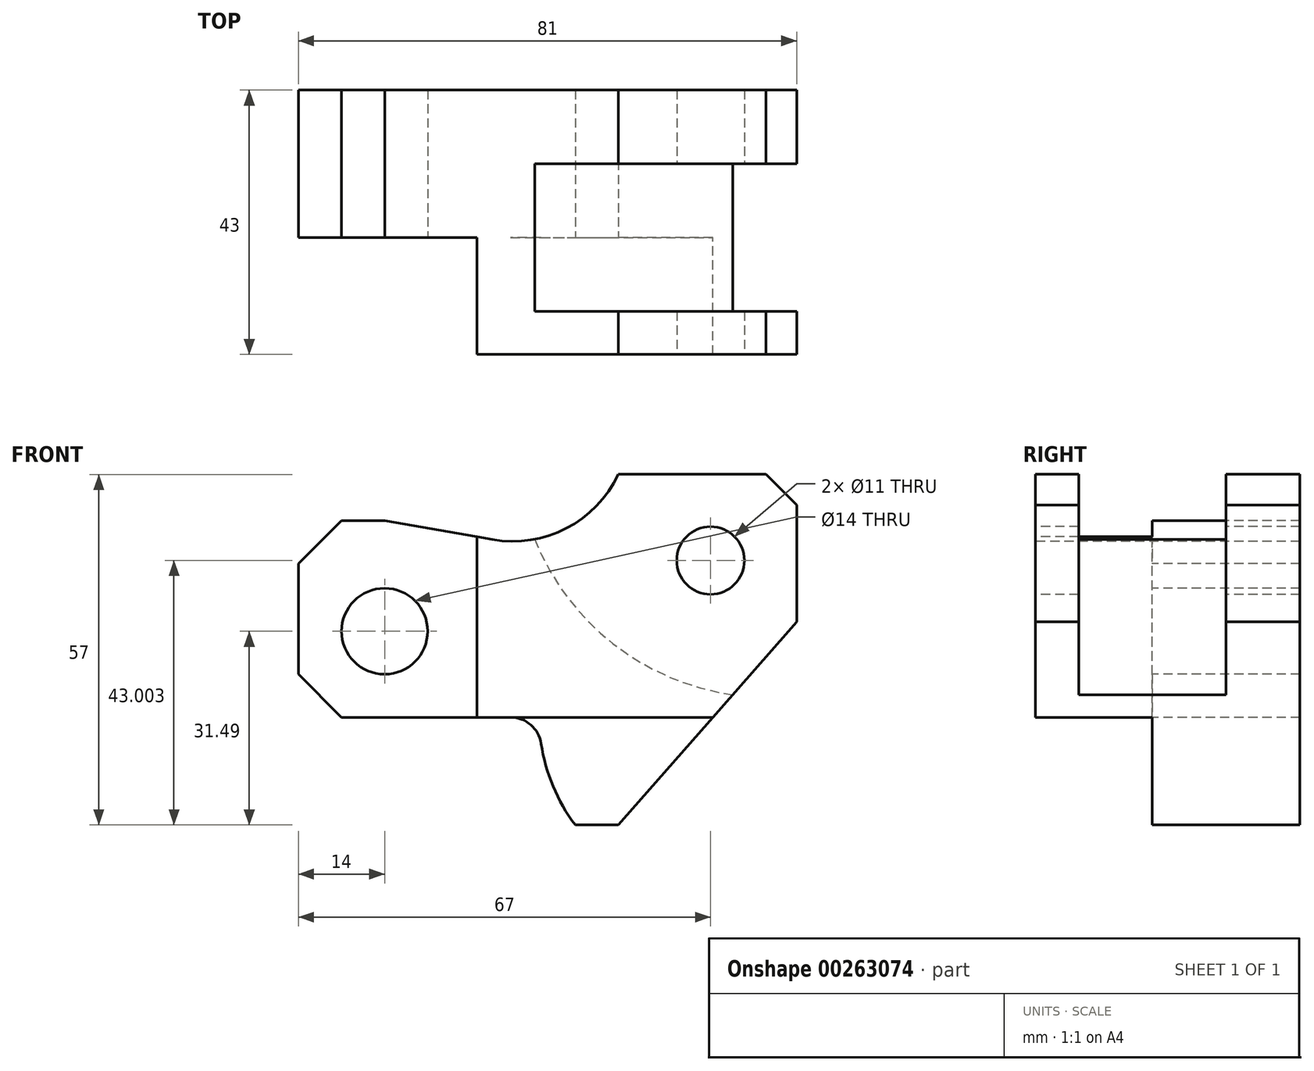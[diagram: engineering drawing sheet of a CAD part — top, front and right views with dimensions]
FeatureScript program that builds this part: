
annotation { "Feature Type Name" : "Feature", "Feature Type Description" : "" }
export const myFeature = defineFeature(function(context is Context, id is Id, definition is map)
    precondition{}
    {
        {
            var Q0;
            Q0=qCreatedBy(makeId("Front.planeOp"),FACE);
            var sketch = newSketch(context, id + "F0", { "sketchPlane" : qUnion([Q0])});
            skCircle(sketch, "E0", {"center": v(0, 0) * mm, "radius": 7 * mm});
            skLineSegment(sketch, "E1", {"start": v(0, 18) * mm, "end": v(-7, 18) * mm});
            skLineSegment(sketch, "E2", {"start": v(-7, -14) * mm, "end": v(-14, -7) * mm});
            skLineSegment(sketch, "E3", {"start": v(-14, -7) * mm, "end": v(-14, 11) * mm});
            skLineSegment(sketch, "E4", {"start": v(-14, 11) * mm, "end": v(-7, 18) * mm});
            skLineSegment(sketch, "E5", {"start": v(38, -31.49) * mm, "end": v(31, -31.49) * mm});
            skArc(sketch, "E6", {"start": v(25.45, -18.26) * mm, "mid": v(27.4, -25.22) * mm, "end": v(31, -31.49) * mm});
            skArc(sketch, "E7", {"start": v(25.45, -18.26) * mm, "mid": v(23.77, -15.21) * mm, "end": v(20.5, -14) * mm});
            skLineSegment(sketch, "E8", {"start": v(-7, -14) * mm, "end": v(20.5, -14) * mm});
            skLineSegment(sketch, "E9", {"start": v(38, -31.49) * mm, "end": v(67, 1.51) * mm});
            skLineSegment(sketch, "E10", {"start": v(67, 1.51) * mm, "end": v(67, 20.51) * mm});
            skLineSegment(sketch, "E11", {"start": v(62, 25.51) * mm, "end": v(67, 20.51) * mm});
            skLineSegment(sketch, "E12", {"start": v(62, 25.51) * mm, "end": v(38, 25.51) * mm});
            skArc(sketch, "E13", {"start": v(17.52, 14.91) * mm, "mid": v(29.55, 16.75) * mm, "end": v(38, 25.51) * mm});
            skLineSegment(sketch, "E14", {"start": v(0, 18) * mm, "end": v(17.52, 14.91) * mm});
            skSolve(sketch);
        }
        {
            var Q0;
            Q0=makeQuery(id+"F0.imprint","IMPRINT",FACE,{"disambiguationData":[TD([[makeQuery(id+"F0.imprint","IMPRINT",EDGE,{"derivedFrom":sQuery(id+"F0.wireOp",EDGE,"E0")}),-1.0]])]});
            extrude(context, id + "F1", {"entities" : qUnion([Q0]), "oppositeDirection" : true, "depth" : 43 * mm});
        }
        {
            var Q0;
            Q0=makeQuery(id+"F1.opExtrude","CAP_FACE",FACE,{"disambiguationData":[OSD([sQuery(id+"F0.wireOp",EDGE,"E0"),sQuery(id+"F0.wireOp",EDGE,"E1"),sQuery(id+"F0.wireOp",EDGE,"E2"),sQuery(id+"F0.wireOp",EDGE,"E3"),sQuery(id+"F0.wireOp",EDGE,"E4"),sQuery(id+"F0.wireOp",EDGE,"E5"),sQuery(id+"F0.wireOp",EDGE,"E6"),sQuery(id+"F0.wireOp",EDGE,"E7"),sQuery(id+"F0.wireOp",EDGE,"E8"),sQuery(id+"F0.wireOp",EDGE,"E9"),sQuery(id+"F0.wireOp",EDGE,"E10"),sQuery(id+"F0.wireOp",EDGE,"E11"),sQuery(id+"F0.wireOp",EDGE,"E12"),sQuery(id+"F0.wireOp",EDGE,"E13"),sQuery(id+"F0.wireOp",EDGE,"E14")])],"isStart":true});
            var sketch = newSketch(context, id + "F2", { "sketchPlane" : qUnion([Q0])});
            skLineSegment(sketch, "E15", {"start": v(-14, -14) * mm, "end": v(-14, -33) * mm});
            skLineSegment(sketch, "E16", {"start": v(-14, -33) * mm, "end": v(67, -33) * mm});
            skLineSegment(sketch, "E17", {"start": v(67, -33) * mm, "end": v(67, -14) * mm});
            skLineSegment(sketch, "E18", {"start": v(67, -14) * mm, "end": v(-14, -14) * mm});
            skSolve(sketch);
        }
        {
            var Q0;
            Q0 = qSketchRegion(id + "F2", true);
            extrude(context, id + "F3", {"entities" : qUnion([Q0]), "operationType" : NewBodyOperationType.REMOVE, "oppositeDirection" : true, "depth" : 19 * mm});
        }
        {
            var Q0;
            Q0=makeQuery(id+"F1.opExtrude","CAP_FACE",FACE,{"disambiguationData":[OSD([sQuery(id+"F0.wireOp",EDGE,"E0"),sQuery(id+"F0.wireOp",EDGE,"E1"),sQuery(id+"F0.wireOp",EDGE,"E2"),sQuery(id+"F0.wireOp",EDGE,"E3"),sQuery(id+"F0.wireOp",EDGE,"E4"),sQuery(id+"F0.wireOp",EDGE,"E5"),sQuery(id+"F0.wireOp",EDGE,"E6"),sQuery(id+"F0.wireOp",EDGE,"E7"),sQuery(id+"F0.wireOp",EDGE,"E8"),sQuery(id+"F0.wireOp",EDGE,"E9"),sQuery(id+"F0.wireOp",EDGE,"E10"),sQuery(id+"F0.wireOp",EDGE,"E11"),sQuery(id+"F0.wireOp",EDGE,"E12"),sQuery(id+"F0.wireOp",EDGE,"E13"),sQuery(id+"F0.wireOp",EDGE,"E14")])],"isStart":true});
            var sketch = newSketch(context, id + "F4", { "sketchPlane" : qUnion([Q0])});
            skLineSegment(sketch, "E19", {"start": v(-14, -14) * mm, "end": v(15, -14) * mm});
            skLineSegment(sketch, "E20", {"start": v(15, -14) * mm, "end": v(15, 23.65) * mm});
            skLineSegment(sketch, "E21", {"start": v(15, 23.65) * mm, "end": v(-14, 23.65) * mm});
            skLineSegment(sketch, "E22", {"start": v(-14, -14) * mm, "end": v(-14, 23.65) * mm});
            skSolve(sketch);
        }
        {
            var Q0;
            Q0 = qSketchRegion(id + "F4", true);
            extrude(context, id + "F5", {"entities" : qUnion([Q0]), "operationType" : NewBodyOperationType.REMOVE, "oppositeDirection" : true, "depth" : 19 * mm});
        }
        {
            var Q0;
            Q0=makeQuery(id+"F1.opExtrude","CAP_FACE",FACE,{"disambiguationData":[OSD([sQuery(id+"F0.wireOp",EDGE,"E0"),sQuery(id+"F0.wireOp",EDGE,"E1"),sQuery(id+"F0.wireOp",EDGE,"E2"),sQuery(id+"F0.wireOp",EDGE,"E3"),sQuery(id+"F0.wireOp",EDGE,"E4"),sQuery(id+"F0.wireOp",EDGE,"E5"),sQuery(id+"F0.wireOp",EDGE,"E6"),sQuery(id+"F0.wireOp",EDGE,"E7"),sQuery(id+"F0.wireOp",EDGE,"E8"),sQuery(id+"F0.wireOp",EDGE,"E9"),sQuery(id+"F0.wireOp",EDGE,"E10"),sQuery(id+"F0.wireOp",EDGE,"E11"),sQuery(id+"F0.wireOp",EDGE,"E12"),sQuery(id+"F0.wireOp",EDGE,"E13"),sQuery(id+"F0.wireOp",EDGE,"E14")])],"isStart":true});
            var sketch = newSketch(context, id + "F6", { "sketchPlane" : qUnion([Q0])});
            skCircle(sketch, "E23", {"center": v(53, 11.51) * mm, "radius": 5.5 * mm});
            skSolve(sketch);
        }
        {
            var Q0;
            Q0 = qSketchRegion(id + "F6", true);
            extrude(context, id + "F7", {"entities" : qUnion([Q0]), "operationType" : NewBodyOperationType.REMOVE, "endBound" : BoundingType.THROUGH_ALL, "oppositeDirection" : true, "depth" : 25 * mm});
        }
        {
            var Q0;
            Q0=makeQuery(id+"F1.opExtrude","CAP_FACE",FACE,{"disambiguationData":[OSD([sQuery(id+"F0.wireOp",EDGE,"E0"),sQuery(id+"F0.wireOp",EDGE,"E1"),sQuery(id+"F0.wireOp",EDGE,"E2"),sQuery(id+"F0.wireOp",EDGE,"E3"),sQuery(id+"F0.wireOp",EDGE,"E4"),sQuery(id+"F0.wireOp",EDGE,"E5"),sQuery(id+"F0.wireOp",EDGE,"E6"),sQuery(id+"F0.wireOp",EDGE,"E7"),sQuery(id+"F0.wireOp",EDGE,"E8"),sQuery(id+"F0.wireOp",EDGE,"E9"),sQuery(id+"F0.wireOp",EDGE,"E10"),sQuery(id+"F0.wireOp",EDGE,"E11"),sQuery(id+"F0.wireOp",EDGE,"E12"),sQuery(id+"F0.wireOp",EDGE,"E13"),sQuery(id+"F0.wireOp",EDGE,"E14")])],"isStart":true});
            cPlane(context, id + "F8", {"entities" : qUnion([Q0]), "cplaneType" : CPlaneType.OFFSET, "offset" : 19 * mm, "oppositeDirection" : true, "width" : 150 * mm, "height" : 150 * mm});
        }
        {
            var Q0;
            Q0=qCreatedBy(id+"F8.planeOp",FACE);
            var sketch = newSketch(context, id + "F9", { "sketchPlane" : qUnion([Q0])});
            skLineSegment(sketch, "E24", {"start": v(67, -10.49) * mm, "end": v(67, 25.51) * mm});
            skArc(sketch, "E25", {"start": v(21.69, 25.67) * mm, "mid": v(36.86, -1.79) * mm, "end": v(67, -10.49) * mm});
            skLineSegment(sketch, "E26", {"start": v(21.69, 25.67) * mm, "end": v(67, 25.51) * mm});
            skSolve(sketch);
        }
        {
            var Q0;
            Q0 = qSketchRegion(id + "F9", true);
            extrude(context, id + "F10", {"entities" : qUnion([Q0]), "operationType" : NewBodyOperationType.REMOVE, "endBound" : BoundingType.SYMMETRIC, "oppositeDirection" : true, "depth" : 24 * mm});
        }
    });
